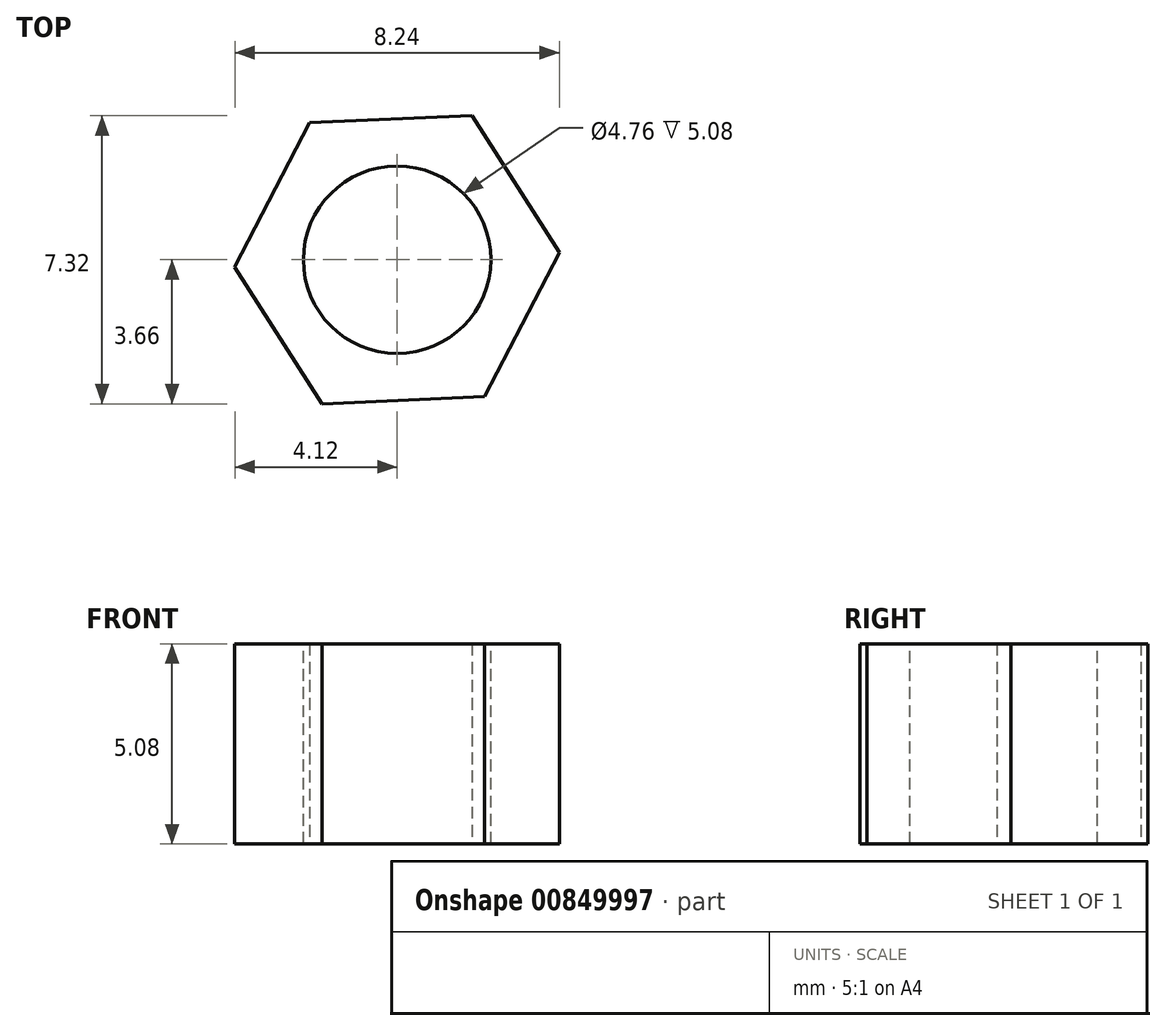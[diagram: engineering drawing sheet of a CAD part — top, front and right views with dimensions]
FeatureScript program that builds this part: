
annotation { "Feature Type Name" : "Feature", "Feature Type Description" : "" }
export const myFeature = defineFeature(function(context is Context, id is Id, definition is map)
    precondition{}
    {
        {
            var Q0;
            Q0=qCreatedBy(makeId("Top.planeOp"),FACE);
            var sketch = newSketch(context, id + "F0", { "sketchPlane" : qUnion([Q0])});
            skCircle(sketch, "E0.cCircle", {"center": v(0, 0) * mm, "radius": 4.13 * mm, "construction": true});
            skLineSegment(sketch, "E0.0", {"start": v(1.9, 3.66) * mm, "end": v(4.12, 0.18) * mm});
            skLineSegment(sketch, "E0.1", {"start": v(4.12, 0.18) * mm, "end": v(2.22, -3.48) * mm});
            skLineSegment(sketch, "E0.2", {"start": v(2.22, -3.48) * mm, "end": v(-1.9, -3.66) * mm});
            skLineSegment(sketch, "E0.3", {"start": v(-1.9, -3.66) * mm, "end": v(-4.12, -0.18) * mm});
            skLineSegment(sketch, "E0.4", {"start": v(-4.12, -0.18) * mm, "end": v(-2.22, 3.48) * mm});
            skLineSegment(sketch, "E0.5", {"start": v(-2.22, 3.48) * mm, "end": v(1.9, 3.66) * mm});
            skSolve(sketch);
        }
        {
            var Q0;
            Q0=makeQuery(id+"F0.imprint","IMPRINT",FACE,{"disambiguationData":[TD([[makeQuery(id+"F0.imprint","IMPRINT",EDGE,{"derivedFrom":sQuery(id+"F0.wireOp",EDGE,"E0.0")}),-1.0]])]});
            extrude(context, id + "F1", {"entities" : qUnion([Q0]), "depth" : 5.08 * mm, "offsetDistance" : 25.4 * mm});
        }
        {
            var Q0;
            Q0=makeQuery(id+"F1.opExtrude","CAP_FACE",FACE,{"disambiguationData":[OSD([sQuery(id+"F0.wireOp",EDGE,"E0.0"),sQuery(id+"F0.wireOp",EDGE,"E0.1"),sQuery(id+"F0.wireOp",EDGE,"E0.2"),sQuery(id+"F0.wireOp",EDGE,"E0.3"),sQuery(id+"F0.wireOp",EDGE,"E0.4"),sQuery(id+"F0.wireOp",EDGE,"E0.5")])],"isStart":false});
            var sketch = newSketch(context, id + "F2", { "sketchPlane" : qUnion([Q0])});
            skCircle(sketch, "E1", {"center": v(0, 0) * mm, "radius": 2.38 * mm});
            skSolve(sketch);
        }
        {
            var Q0;
            Q0=makeQuery(id+"F2.imprint","IMPRINT",FACE,{"disambiguationData":[TD([[makeQuery(id+"F2.imprint","IMPRINT",EDGE,{"derivedFrom":sQuery(id+"F2.wireOp",EDGE,"E1")}),1.0]])]});
            extrude(context, id + "F3", {"entities" : qUnion([Q0]), "operationType" : NewBodyOperationType.REMOVE, "endBound" : BoundingType.THROUGH_ALL, "oppositeDirection" : true, "depth" : 25.4 * mm, "offsetDistance" : 25.4 * mm});
        }
    });
